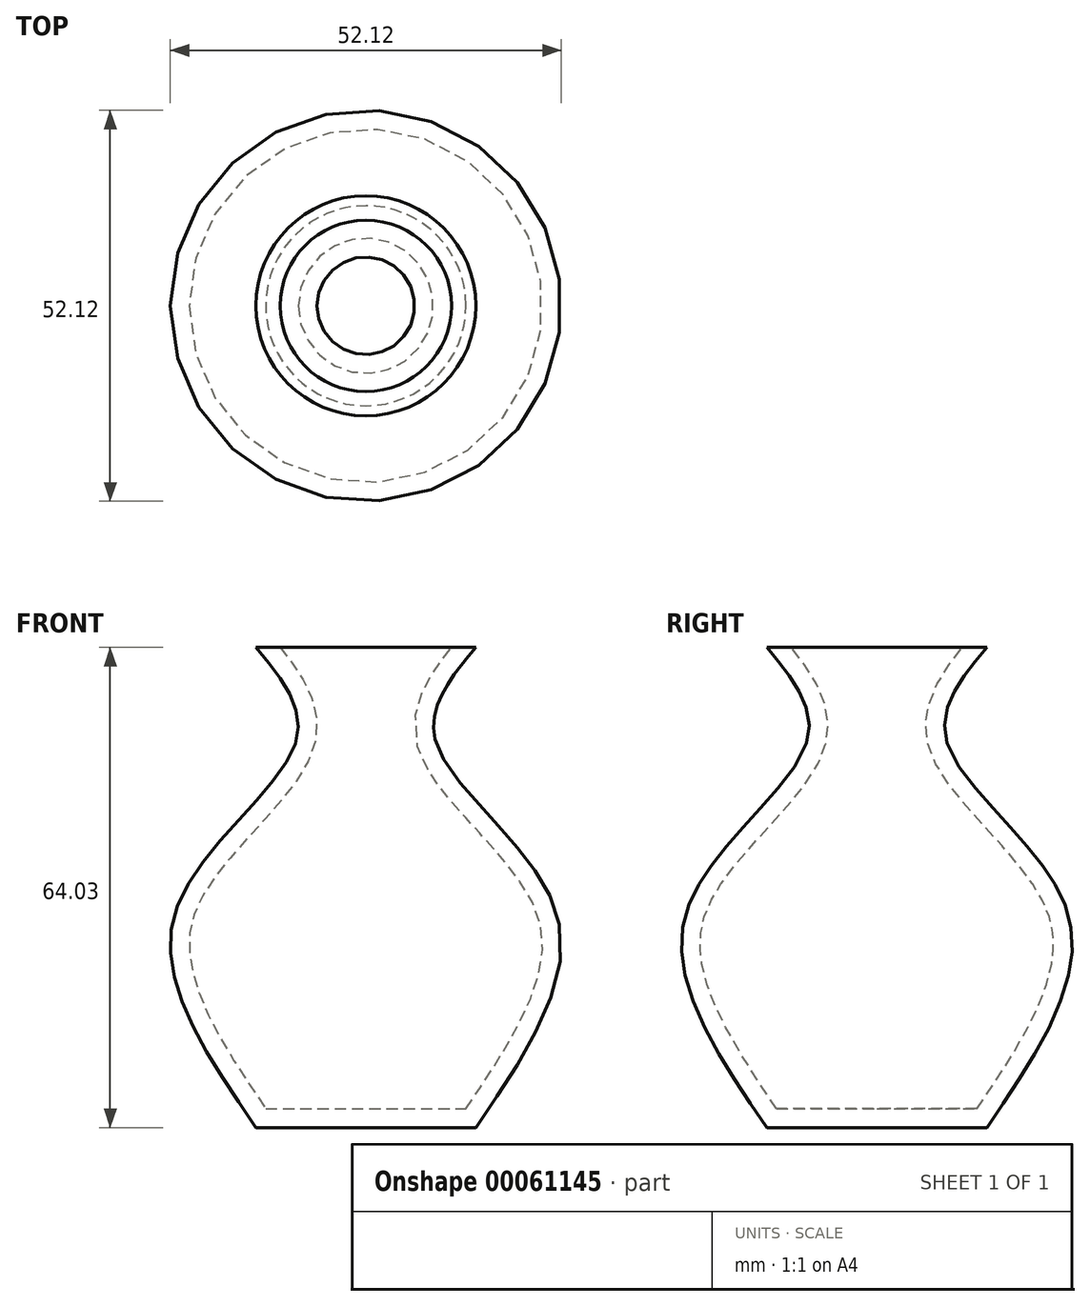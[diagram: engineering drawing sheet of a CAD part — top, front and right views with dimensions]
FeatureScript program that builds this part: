
annotation { "Feature Type Name" : "Feature", "Feature Type Description" : "" }
export const myFeature = defineFeature(function(context is Context, id is Id, definition is map)
    precondition{}
    {
        {
            var Q0;
            Q0=qCreatedBy(makeId("Front.planeOp"),FACE);
            var sketch = newSketch(context, id + "F0", { "sketchPlane" : qUnion([Q0])});
            skLineSegment(sketch, "E0", {"start": v(32.97, 39.66) * mm, "end": v(47.64, 39.66) * mm});
            skFitSpline(sketch, "E1", {"points": [v(47.64, 39.66) * mm, v(42.28, 27.09) * mm, v(58.35, 4.5) * mm, v(47.64, -24.37) * mm], "startDerivative": vector(-39.44, -47.2) * mm, "endDerivative": vector(-53.28, -78.1) * mm});
            skLineSegment(sketch, "E2", {"start": v(47.64, -24.37) * mm, "end": v(32.97, -24.37) * mm});
            skLineSegment(sketch, "E3", {"start": v(32.97, -24.37) * mm, "end": v(32.97, 39.66) * mm});
            skSolve(sketch);
        }
        {
            var Q0;
            Q0 = qSketchRegion(id + "F0", true);
            var Q1;
            Q1=sQuery(id+"F0.wireOp",EDGE,"E3");
            revolve(context, id + "F1", {"entities" : qUnion([Q0]), "axis" : qUnion([Q1]), "revolveType" : RevolveType.FULL});
        }
        {
            var Q0;
            Q0=makeQuery(id+"F1.opRevolve","SWEPT_FACE",FACE,{"disambiguationData":[OSD([sQuery(id+"F0.wireOp",EDGE,"E0")])]});
            shell(context, id + "F2", {"entities" : qUnion([Q0]), "thickness" : 2.5 * mm});
        }
    });
